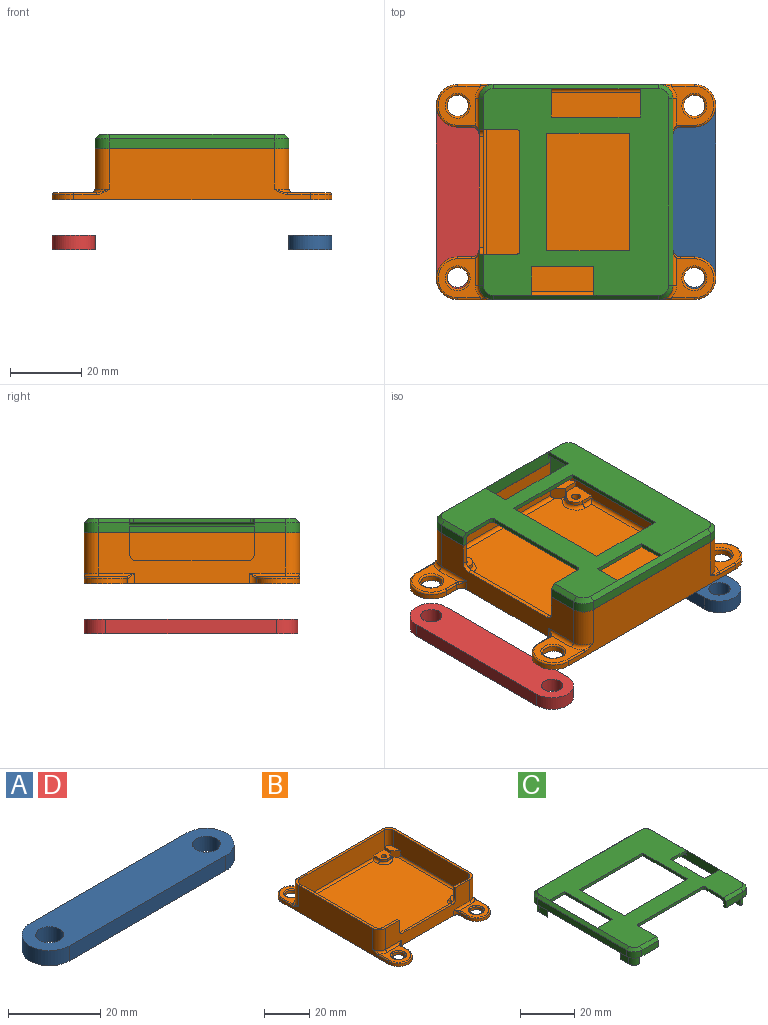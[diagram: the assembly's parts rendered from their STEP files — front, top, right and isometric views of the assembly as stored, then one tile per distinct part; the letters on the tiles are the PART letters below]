
ASSEMBLY  parts=4 mates=3
PART A: 8 faces, bbox 60x12x4 mm
  f0: cylinder r=6mm len=12mm, axis (0,0,-1), area 75.4mm2, adj f1,f3,f6,f7
  f1: plane 48x4mm, normal (0,1,0), area 192mm2, adj f0,f2,f6,f7
  f2: cylinder r=6mm len=12mm, axis (0,0,-1), area 75.4mm2, adj f1,f3,f6,f7
  f3: plane 48x4mm, normal (0,-1,0), area 192mm2, adj f0,f2,f6,f7
  f4: cylinder r=3mm len=6mm, axis (0,0,-1), area 75.4mm2, adj f6,f7
  f5: cylinder r=3mm len=6mm, axis (0,0,-1), area 75.4mm2, adj f6,f7
  f6: plane 60x12mm, normal (0,0,1), area 632.5mm2, adj f0,f1,f2,f3,f4,f5
  f7: plane 60x12mm, normal (0,0,-1), area 632.5mm2, adj f0,f1,f2,f3,f4,f5
PART B: 136 faces, bbox 64.9x79.5x14.4 mm
  f0: plane 52.5x11.4mm, normal (0,1,0), area 306.6mm2, adj f33,f34,f38,f42,f43,f44,f48,f71
  f1: plane 46.5x11.4mm, normal (-1,0,0), area 508.1mm2, adj f32,f33,f38,f77,f78,f80,f81,f134
  f2: plane 52.5x14.4mm, normal (0,-1,0), area 417.7mm2, adj f27,f28,f37,f38,f60,f66,f69,f70
  f3: plane 56.1x50.1mm, normal (0,0,1), area 2612.6mm2, adj f77,f80,f83,f86,f116,f118,f119,f120
  f4: plane 11.93x11.21mm, normal (0,0,1), area 65.7mm2, adj f59,f60,f95,f96,f97,f98,f113
  f5: plane 11.93x11.21mm, normal (0,0,1), area 65.7mm2, adj f61,f62,f101,f102,f103,f104,f114
  f6: plane 11.93x11.21mm, normal (0,0,1), area 65.7mm2, adj f65,f66,f89,f90,f91,f92,f112
  f7: plane 66.5x14.4mm, normal (-1,0,0), area 703.5mm2, adj f8,f24,f27,f30,f37,f38,f88,f89
  f8: cylinder r=6mm len=12mm, axis (0,0,-1), area 28.3mm2, adj f7,f9,f27,f90
  f9: plane 4x1.5mm, normal (1,0,0), area 6mm2, adj f8,f27,f69,f91
  f10: plane 4x1.5mm, normal (-1,0,0), area 6mm2, adj f11,f27,f70,f97
  f11: cylinder r=6mm len=12mm, axis (0,0,-1), area 28.3mm2, adj f10,f12,f27,f96
  f12: plane 66.5x14.4mm, normal (1,0,0), area 703.5mm2, adj f11,f13,f27,f28,f29,f38,f94,f95
  f13: cylinder r=6mm len=12mm, axis (0,0,-1), area 28.3mm2, adj f12,f14,f27,f102
  f14: plane 4x1.5mm, normal (-1,0,0), area 6mm2, adj f13,f27,f68,f103
  f15: plane 52.5x14.4mm, normal (0,1,0), area 696mm2, adj f27,f29,f30,f38,f62,f64,f67,f68
  f16: plane 4x1.5mm, normal (1,0,0), area 6mm2, adj f24,f27,f67,f109
  f17: cylinder r=1.25mm len=4mm, axis (0,0,-1), area 31.4mm2, adj f27,f58
  f18: cylinder r=1.25mm len=4mm, axis (0,0,-1), area 31.4mm2, adj f27,f48
  f19: cylinder r=1.25mm len=4mm, axis (0,0,-1), area 31.4mm2, adj f27,f53
  f20: cylinder r=3mm len=6mm, axis (0,0,-1), area 28.3mm2, adj f27,f113
  f21: cylinder r=3mm len=6mm, axis (0,0,-1), area 28.3mm2, adj f27,f112
  f22: cylinder r=3mm len=6mm, axis (0,0,-1), area 28.3mm2, adj f27,f114
  f23: cylinder r=3mm len=6mm, axis (0,0,-1), area 28.3mm2, adj f27,f115
  f24: cylinder r=6mm len=12mm, axis (0,0,-1), area 28.3mm2, adj f7,f16,f27,f108
  f25: cylinder r=1.25mm len=4mm, axis (0,0,-1), area 31.4mm2, adj f27,f43
  f26: plane 11.93x11.21mm, normal (0,0,1), area 65.7mm2, adj f63,f64,f107,f108,f109,f110,f115
  f27: plane 78.5x60.5mm, normal (0,0,-1), area 3682.1mm2, adj f2,f7,f8,f9,f10,f11,f12,f13
  f28: cylinder r=4mm len=11.4mm, axis (0,0,-1), area 71.6mm2, adj f2,f12,f38,f59
  f29: cylinder r=4mm len=11.4mm, axis (0,0,-1), area 71.6mm2, adj f12,f15,f38,f61
  f30: cylinder r=4mm len=11.4mm, axis (0,0,-1), area 71.6mm2, adj f7,f15,f38,f63
  f31: plane 52.5x11.4mm, normal (0,-1,0), area 584.9mm2, adj f32,f36,f38,f49,f53,f57,f58,f76
  f32: cylinder r=2.8mm len=8.9mm, axis (0,0,-1), area 39.1mm2, adj f1,f31,f38,f78
  f33: cylinder r=2.8mm len=8.9mm, axis (0,0,-1), area 39.1mm2, adj f0,f1,f38,f81
  f34: cylinder r=2.8mm len=8.9mm, axis (0,0,-1), area 39.1mm2, adj f0,f35,f38,f84
  f35: plane 46.5x11.4mm, normal (1,0,0), area 508mm2, adj f34,f36,f38,f83,f84,f86,f87,f135
  f36: cylinder r=2.8mm len=8.9mm, axis (0,0,-1), area 39.1mm2, adj f31,f35,f38,f87
  f37: cylinder r=4mm len=11.4mm, axis (0,0,-1), area 71.6mm2, adj f2,f7,f38,f65
  f38: plane 60.5x54.5mm, normal (0,0,1), area 221.2mm2, adj f0,f1,f2,f7,f12,f15,f28,f29
  f39: plane 1x0.19mm, normal (0,1,0), area 0.2mm2, adj f40,f43,f80,f125
  f40: cylinder r=1mm len=1mm, axis (0,0,-1), area 1.1mm2, adj f39,f41,f43,f126
  f41: cylinder r=2.75mm len=5.22mm, axis (0,0,-1), area 7.4mm2, adj f40,f42,f43,f127
  f42: plane 3.55x1mm, normal (-1,0,0), area 3.6mm2, adj f0,f41,f43,f128
  f43: plane 6.3x6.3mm, normal (0,0,1), area 30mm2, adj f0,f25,f39,f40,f41,f42,f79
  f44: plane 3.55x1mm, normal (1,0,0), area 3.6mm2, adj f0,f45,f48,f130
  f45: cylinder r=2.75mm len=5.22mm, axis (0,0,-1), area 7.4mm2, adj f44,f46,f48,f131
  f46: cylinder r=1mm len=1mm, axis (0,0,-1), area 1.1mm2, adj f45,f47,f48,f132
  f47: plane 1x0.19mm, normal (0,1,0), area 0.2mm2, adj f46,f48,f83,f133
  f48: plane 6.3x6.3mm, normal (0,0,1), area 30mm2, adj f0,f18,f44,f45,f46,f47,f82
  f49: plane 3.55x1mm, normal (-1,0,0), area 3.6mm2, adj f31,f50,f53,f119
  f50: cylinder r=2.75mm len=5.22mm, axis (0,0,-1), area 7.4mm2, adj f49,f51,f53,f118
  f51: cylinder r=1mm len=1mm, axis (0,0,-1), area 1.1mm2, adj f50,f52,f53,f117
  f52: plane 1x0.19mm, normal (0,-1,0), area 0.2mm2, adj f51,f53,f77,f116
  f53: plane 6.3x6.3mm, normal (0,0,1), area 30mm2, adj f19,f31,f49,f50,f51,f52,f76
  f54: plane 1x0.19mm, normal (0,-1,0), area 0.2mm2, adj f55,f58,f86,f124
  f55: cylinder r=1mm len=1mm, axis (0,0,-1), area 1.1mm2, adj f54,f56,f58,f123
  f56: cylinder r=2.75mm len=5.22mm, axis (0,0,-1), area 7.4mm2, adj f55,f57,f58,f122
  f57: plane 3.55x1mm, normal (1,0,0), area 3.6mm2, adj f31,f56,f58,f121
  f58: plane 6.3x6.3mm, normal (0,0,1), area 30mm2, adj f17,f31,f54,f55,f56,f57,f85
  f59: torus R=5mm, axis (0,0,1), area 7.6mm2, adj f4,f28,f60,f94
  f60: cylinder r=1mm len=10mm, axis (-1,0,0), area 13.6mm2, adj f2,f4,f59,f99
  f61: torus R=5mm, axis (0,0,1), area 7.6mm2, adj f5,f29,f62,f100
  f62: cylinder r=1mm len=10mm, axis (1,0,0), area 13.6mm2, adj f5,f15,f61,f105
  f63: torus R=5mm, axis (0,0,1), area 7.6mm2, adj f26,f30,f64,f106
  f64: cylinder r=1mm len=10mm, axis (1,0,0), area 13.6mm2, adj f15,f26,f63,f111
  f65: torus R=5mm, axis (0,0,1), area 7.6mm2, adj f6,f37,f66,f88
  f66: cylinder r=1mm len=10mm, axis (-1,0,0), area 13.6mm2, adj f2,f6,f65,f93
  f67: cylinder r=2mm len=3mm, axis (0,0,-1), area 6mm2, adj f15,f16,f27,f110,f111
  f68: cylinder r=2mm len=3mm, axis (0,0,1), area 6mm2, adj f14,f15,f27,f104,f105
  f69: cylinder r=2mm len=3mm, axis (0,0,-1), area 6mm2, adj f2,f9,f27,f92,f93
  f70: cylinder r=2mm len=3mm, axis (0,0,1), area 6mm2, adj f2,f10,f27,f98,f99
  f71: plane 6x1.2mm, normal (1,0,0), area 7.2mm2, adj f0,f2,f38,f72
  f72: cylinder r=2mm len=2mm, axis (0,-1,0), area 3.8mm2, adj f0,f2,f71,f74
  f73: cylinder r=2mm len=2mm, axis (0,-1,0), area 3.8mm2, adj f0,f2,f74,f75
  f74: plane 31x1.2mm, normal (0,0,1), area 37.2mm2, adj f0,f2,f72,f73
  f75: plane 6x1.2mm, normal (-1,0,0), area 7.2mm2, adj f0,f2,f38,f73
  f76: plane 4.21x1.5mm, normal (-1,0,0), area 6.3mm2, adj f31,f53,f77,f78
  f77: plane 3.5x3mm, normal (-0.71,-0.71,0), area 14.2mm2, adj f1,f3,f52,f76,f78,f116,f134
  f78: plane 7.21x3mm, normal (0,0,1), area 15.4mm2, adj f1,f31,f32,f76,f77
  f79: plane 4.21x1.5mm, normal (-1,0,0), area 6.3mm2, adj f0,f43,f80,f81
  f80: plane 3.5x3mm, normal (-0.71,0.71,0), area 14.2mm2, adj f1,f3,f39,f79,f81,f125,f134
  f81: plane 7.21x3mm, normal (0,0,1), area 15.4mm2, adj f0,f1,f33,f79,f80
  f82: plane 4.21x1.5mm, normal (1,0,0), area 6.3mm2, adj f0,f48,f83,f84
  f83: plane 3.5x3mm, normal (0.71,0.71,0), area 14.2mm2, adj f3,f35,f47,f82,f84,f133,f135
  f84: plane 7.21x3mm, normal (0,0,1), area 15.4mm2, adj f0,f34,f35,f82,f83
  f85: plane 4.21x1.5mm, normal (1,0,0), area 6.3mm2, adj f31,f58,f86,f87
  f86: plane 3.5x3mm, normal (0.71,-0.71,0), area 14.2mm2, adj f3,f35,f54,f85,f87,f124,f135
  f87: plane 7.21x3mm, normal (0,0,1), area 15.4mm2, adj f31,f35,f36,f85,f86
  f88: bspline ~4.08x1.5mm, area 1.5mm2, adj f7,f65,f89
  f89: cylinder r=0.5mm len=6.43mm, axis (0,1,0), area 5mm2, adj f6,f7,f88,f90
  f90: torus R=5.5mm, axis (0,0,1), area 14.4mm2, adj f6,f8,f89,f91
  f91: cylinder r=0.5mm len=4mm, axis (0,-1,0), area 3.1mm2, adj f6,f9,f90,f92
  f92: torus R=2.5mm, axis (0,0,1), area 0.7mm2, adj f6,f69,f91,f93
  f93: bspline ~2.4x1.5mm, area 1.1mm2, adj f66,f69,f92
  f94: bspline ~4.08x1.5mm, area 1.5mm2, adj f12,f59,f95
  f95: cylinder r=0.5mm len=6.43mm, axis (0,-1,0), area 5mm2, adj f4,f12,f94,f96
  f96: torus R=5.5mm, axis (0,0,1), area 14.4mm2, adj f4,f11,f95,f97
  f97: cylinder r=0.5mm len=4mm, axis (0,1,0), area 3.1mm2, adj f4,f10,f96,f98
  f98: torus R=2.5mm, axis (0,0,1), area 0.7mm2, adj f4,f70,f97,f99
  f99: bspline ~2.4x1.5mm, area 1.1mm2, adj f60,f70,f98
  f100: bspline ~4.08x1.5mm, area 1.5mm2, adj f12,f61,f101
  f101: cylinder r=0.5mm len=6.43mm, axis (0,-1,0), area 5mm2, adj f5,f12,f100,f102
  f102: torus R=5.5mm, axis (0,0,1), area 14.4mm2, adj f5,f13,f101,f103
  f103: cylinder r=0.5mm len=4mm, axis (0,1,0), area 3.1mm2, adj f5,f14,f102,f104
  f104: torus R=2.5mm, axis (0,0,1), area 0.7mm2, adj f5,f68,f103,f105
  f105: bspline ~2.4x1.5mm, area 1.1mm2, adj f62,f68,f104
  f106: bspline ~4.08x1.5mm, area 1.5mm2, adj f7,f63,f107
  f107: cylinder r=0.5mm len=6.43mm, axis (0,1,0), area 5mm2, adj f7,f26,f106,f108
  f108: torus R=5.5mm, axis (0,0,1), area 14.4mm2, adj f24,f26,f107,f109
  f109: cylinder r=0.5mm len=4mm, axis (0,-1,0), area 3.1mm2, adj f16,f26,f108,f110
  f110: torus R=2.5mm, axis (0,0,1), area 0.7mm2, adj f26,f67,f109,f111
  f111: bspline ~2.4x1.5mm, area 1.1mm2, adj f64,f67,f110
  f112: torus R=3.5mm, axis (0,0,1), area 15.7mm2, adj f6,f21
  f113: torus R=3.5mm, axis (0,0,1), area 15.7mm2, adj f4,f20
  f114: torus R=3.5mm, axis (0,0,1), area 15.7mm2, adj f5,f22
  f115: torus R=3.5mm, axis (0,0,1), area 15.7mm2, adj f23,f26
  f116: cylinder r=1mm len=1.19mm, axis (-1,0,0), area 0.9mm2, adj f3,f52,f77,f117
  f117: sphere r=1mm, area 1.1mm2, adj f51,f116,f118
  f118: torus R=3.75mm, axis (0,0,1), area 13.1mm2, adj f3,f50,f117,f119
  f119: cylinder r=1mm len=3.55mm, axis (0,1,0), area 5mm2, adj f3,f49,f118,f120
  f120: cylinder r=1mm len=39.5mm, axis (-1,0,0), area 60.9mm2, adj f3,f31,f119,f121
  f121: cylinder r=1mm len=3.55mm, axis (0,-1,0), area 5mm2, adj f3,f57,f120,f122
  f122: torus R=3.75mm, axis (0,0,1), area 13.1mm2, adj f3,f56,f121,f123
  f123: sphere r=1mm, area 1.1mm2, adj f55,f122,f124
  f124: cylinder r=1mm len=1.19mm, axis (-1,0,0), area 0.9mm2, adj f3,f54,f86,f123
  f125: cylinder r=1mm len=1.19mm, axis (1,0,0), area 0.9mm2, adj f3,f39,f80,f126
  f126: sphere r=1mm, area 1.1mm2, adj f40,f125,f127
  f127: torus R=3.75mm, axis (0,0,1), area 13.1mm2, adj f3,f41,f126,f128
  f128: cylinder r=1mm len=3.55mm, axis (0,1,0), area 5mm2, adj f3,f42,f127,f129
  f129: cylinder r=1mm len=39.5mm, axis (1,0,0), area 60.9mm2, adj f0,f3,f128,f130
  f130: cylinder r=1mm len=3.55mm, axis (0,-1,0), area 5mm2, adj f3,f44,f129,f131
  f131: torus R=3.75mm, axis (0,0,1), area 13.1mm2, adj f3,f45,f130,f132
  f132: sphere r=1mm, area 1.1mm2, adj f46,f131,f133
  f133: cylinder r=1mm len=1.19mm, axis (1,0,0), area 0.9mm2, adj f3,f47,f83,f132
  f134: cylinder r=1mm len=39.68mm, axis (0,1,0), area 60.3mm2, adj f1,f3,f77,f80
  f135: cylinder r=1mm len=39.68mm, axis (0,-1,0), area 60.3mm2, adj f3,f35,f83,f86
PART C: 72 faces, bbox 60.5x54.5x8 mm
  f0: plane 56.1x50.1mm, normal (0,0,-1), area 1385.5mm2, adj f2,f3,f5,f6,f21,f22,f23,f24
  f1: plane 37.68x4mm, normal (1,0,0), area 122.8mm2, adj f3,f10,f31,f32,f40,f45,f62,f70
  f2: cylinder r=1mm len=52.1mm, axis (-1,0,0), area 81.8mm2, adj f0,f8,f50,f66
  f3: cylinder r=1mm len=1.79mm, axis (0,-1,0), area 1.8mm2, adj f0,f1,f31,f70
  f4: plane 8.55x1.8mm, normal (0,1,0), area 15.4mm2, adj f5,f10,f26,f55
  f5: cylinder r=1mm len=8.55mm, axis (1,0,0), area 13.4mm2, adj f0,f4,f26,f55
  f6: cylinder r=1mm len=7.39mm, axis (0,1,0), area 10.6mm2, adj f0,f7,f23,f58
  f7: plane 37.68x4mm, normal (-1,0,0), area 106.3mm2, adj f6,f10,f21,f23,f36,f43,f48,f58
  f8: plane 52.1x1.8mm, normal (0,-1,0), area 93.8mm2, adj f2,f10,f50,f66
  f9: plane 8.75x2.8mm, normal (0,-1,0), area 24.5mm2, adj f10,f12,f26,f34
  f10: plane 60.5x54.5mm, normal (0,0,-1), area 221.2mm2, adj f1,f4,f7,f8,f9,f11,f12,f13
  f11: plane 8.75x2.8mm, normal (0,-1,0), area 24.5mm2, adj f10,f18,f25,f42
  f12: cylinder r=4mm len=4mm, axis (0,0,-1), area 17.6mm2, adj f9,f10,f13,f35
  f13: plane 46.5x2.8mm, normal (1,0,0), area 130.2mm2, adj f10,f12,f14,f36
  f14: cylinder r=4mm len=4mm, axis (0,0,-1), area 17.6mm2, adj f10,f13,f15,f37
  f15: plane 52.5x2.8mm, normal (0,1,0), area 147mm2, adj f10,f14,f16,f38
  f16: cylinder r=4mm len=4mm, axis (0,0,-1), area 17.6mm2, adj f10,f15,f17,f39
  f17: plane 46.5x2.8mm, normal (-1,0,0), area 130.2mm2, adj f10,f16,f18,f40
  f18: cylinder r=4mm len=4mm, axis (0,0,-1), area 17.6mm2, adj f10,f11,f17,f41
  f19: plane 58.1x52.1mm, normal (0,0,1), area 1551.3mm2, adj f21,f22,f23,f24,f25,f26,f27,f28
  f20: plane 8.55x1.8mm, normal (0,1,0), area 15.4mm2, adj f10,f25,f44,f61
  f21: plane 8x2.2mm, normal (0,-1,0), area 9.8mm2, adj f0,f7,f19,f22,f43
  f22: plane 17.5x1.2mm, normal (1,0,0), area 21mm2, adj f0,f19,f21,f23
  f23: plane 8x2.2mm, normal (0,1,0), area 9.8mm2, adj f0,f6,f7,f19,f22
  f24: plane 33x1.2mm, normal (0,-1,0), area 39.6mm2, adj f0,f19,f46,f47
  f25: plane 10.5x4mm, normal (1,0,0), area 15.5mm2, adj f0,f10,f11,f19,f20,f42,f44,f47
  f26: plane 10.5x4mm, normal (-1,0,0), area 15.5mm2, adj f0,f4,f5,f9,f10,f19,f34,f46
  f27: plane 23.3x1.2mm, normal (-1,0,0), area 28mm2, adj f0,f19,f28,f30
  f28: plane 33x1.2mm, normal (0,-1,0), area 39.6mm2, adj f0,f19,f27,f29
  f29: plane 23.3x1.2mm, normal (1,0,0), area 28mm2, adj f0,f19,f28,f30
  f30: plane 33x1.2mm, normal (0,1,0), area 39.6mm2, adj f0,f19,f27,f29
  f31: plane 8x2.2mm, normal (0,-1,0), area 9.8mm2, adj f0,f1,f3,f19,f33
  f32: plane 8x2.2mm, normal (0,1,0), area 9.8mm2, adj f0,f1,f19,f33,f45
  f33: plane 25x1.2mm, normal (-1,0,0), area 30mm2, adj f0,f19,f31,f32
  f34: plane 8.75x1.2mm, normal (0,-0.71,0.71), area 14.8mm2, adj f9,f19,f26,f35
  f35: cone r=2.8mm half-angle=45deg, axis (0,0,-1), area 9.1mm2, adj f12,f19,f34,f36
  f36: plane 46.5x1.2mm, normal (0.71,0,0.71), area 78.9mm2, adj f7,f13,f19,f35,f37
  f37: cone r=2.8mm half-angle=45deg, axis (0,0,-1), area 9.1mm2, adj f14,f19,f36,f38
  f38: plane 52.5x1.2mm, normal (0,0.71,0.71), area 89.1mm2, adj f15,f19,f37,f39
  f39: cone r=2.8mm half-angle=45deg, axis (0,0,-1), area 9.1mm2, adj f16,f19,f38,f40
  f40: plane 46.5x1.2mm, normal (-0.71,0,0.71), area 78.9mm2, adj f1,f17,f19,f39,f41
  f41: cone r=2.8mm half-angle=45deg, axis (0,0,-1), area 9.1mm2, adj f18,f19,f40,f42
  f42: plane 8.75x1.2mm, normal (0,-0.71,0.71), area 14.8mm2, adj f11,f19,f25,f41
  f43: cylinder r=1mm len=14.79mm, axis (0,1,0), area 22.2mm2, adj f0,f7,f21,f48
  f44: cylinder r=1mm len=8.55mm, axis (1,0,0), area 13.4mm2, adj f0,f20,f25,f61
  f45: cylinder r=1mm len=12.89mm, axis (0,-1,0), area 19.2mm2, adj f0,f1,f32,f62
  f46: cylinder r=1mm len=1.2mm, axis (0,0,-1), area 1.9mm2, adj f0,f19,f24,f26
  f47: cylinder r=1mm len=1.2mm, axis (0,0,1), area 1.9mm2, adj f0,f19,f24,f25
  f48: plane 6.8x3mm, normal (-0.71,-0.71,0), area 28.5mm2, adj f0,f7,f43,f49,f50,f53
  f49: plane 4.41x4mm, normal (1,0,0), area 17.6mm2, adj f10,f48,f51,f53
  f50: plane 6.8x4.21mm, normal (-1,0,0), area 28.4mm2, adj f0,f2,f8,f48,f52,f53
  f51: cylinder r=2.8mm len=4mm, axis (0,0,1), area 17.6mm2, adj f10,f49,f52,f53
  f52: plane 4x0.2mm, normal (0,1,0), area 0.8mm2, adj f10,f50,f51,f53
  f53: plane 7.21x3mm, normal (0,0,-1), area 15.4mm2, adj f48,f49,f50,f51,f52
  f54: plane 4x0.2mm, normal (0,-1,0), area 0.8mm2, adj f10,f55,f56,f59
  f55: plane 6.8x4.21mm, normal (-1,0,0), area 28.4mm2, adj f0,f4,f5,f54,f58,f59
  f56: cylinder r=2.8mm len=4mm, axis (0,0,1), area 17.6mm2, adj f10,f54,f57,f59
  f57: plane 4.41x4mm, normal (1,0,0), area 17.6mm2, adj f10,f56,f58,f59
  f58: plane 6.8x3mm, normal (-0.71,0.71,0), area 28.5mm2, adj f0,f6,f7,f55,f57,f59
  f59: plane 7.21x3mm, normal (0,0,-1), area 15.4mm2, adj f54,f55,f56,f57,f58
  f60: plane 4x0.2mm, normal (0,-1,0), area 0.8mm2, adj f10,f61,f64,f65
  f61: plane 6.8x4.21mm, normal (1,0,0), area 28.4mm2, adj f0,f20,f44,f60,f62,f65
  f62: plane 6.8x3mm, normal (0.71,0.71,0), area 28.5mm2, adj f0,f1,f45,f61,f63,f65
  f63: plane 4.41x4mm, normal (-1,0,0), area 17.6mm2, adj f10,f62,f64,f65
  f64: cylinder r=2.8mm len=4mm, axis (0,0,1), area 17.6mm2, adj f10,f60,f63,f65
  f65: plane 7.21x3mm, normal (0,0,-1), area 15.4mm2, adj f60,f61,f62,f63,f64
  f66: plane 6.8x4.21mm, normal (1,0,0), area 28.4mm2, adj f0,f2,f8,f67,f70,f71
  f67: plane 4x0.2mm, normal (0,1,0), area 0.8mm2, adj f10,f66,f68,f71
  f68: cylinder r=2.8mm len=4mm, axis (0,0,1), area 17.6mm2, adj f10,f67,f69,f71
  f69: plane 4.41x4mm, normal (-1,0,0), area 17.6mm2, adj f10,f68,f70,f71
  f70: plane 6.8x3mm, normal (0.71,-0.71,0), area 28.5mm2, adj f0,f1,f3,f66,f69,f71
  f71: plane 7.21x3mm, normal (0,0,-1), area 15.4mm2, adj f66,f67,f68,f69,f70
PART D: same geometry as A
PLACE A rot(axis=(0.71,0.71,0),180deg) t=(61.05,-66.77,14.44)mm
PLACE B rot(axis=(0,0,-1),90deg) t=(27.8,-67.02,24.44)mm
PLACE C rot(axis=(0,0,-1),90deg) t=(27.8,-67.02,38.8)mm
PLACE D rot(axis=(0.71,0.71,0),180deg) t=(-5.45,-66.77,14.44)mm
MATE fastened B.f8 <-> D.f0  axis (0,0,-1) through (-5.45,-42.77,24.44)mm
MATE fastened B.f23 <-> A.f0  axis (0,0,-1) through (61.05,-42.77,24.44)mm
MATE slider B.f38 <-> C.f10  axis (0,0,1) through (0.55,-40.77,38.84)mm
